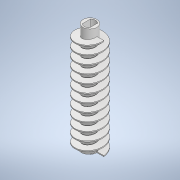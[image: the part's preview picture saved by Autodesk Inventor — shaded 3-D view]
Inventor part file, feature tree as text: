
AUTODESK INVENTOR PART (.ipt)
format: ipt  version: 2022 (Build 260153000, 153)  size: 613,888 bytes
history: native  units: mm
features: sketch x7, extrude x5, other x4, projected_geometry x3, reference x2, mirror x1, sweep x1, chamfer x1
ambient origin geometry x8: Origin, YZ Plane, XZ Plane, XY Plane, X Axis, Y Axis, Z Axis, Center Point
bodies: Solid1 (feature_tree)
feature tree (24):
  extrude  "Extrusion1"  Depth=10.0mm
  sketch  "3D Sketch1"
  extrude  "Extrusion2"  Depth=50.5mm
  mirror  "Mirror1"
  sweep  "Sweep1"
  chamfer  "Chamfer1"  Distance=3.5mm Angle=45.0deg
  extrude  "Extrusion3"  Depth=3.3mm
  extrude  "Extrusion4"  Depth=0.3mm
  extrude  "Extrusion6"  Depth=5.0mm TaperAngle=0.0deg
  sketch  "Sketch1"  dims[d2=0.0mm d3=10.0mm]
  other  "Helical Curve1"
  sketch  "Sketch2"  dims[d6=0.0mm d7=50.5mm]
  projected_geometry  "Projected Loop1"
  sketch  "Sketch3"  dims[d9=0.0mm d10=0.0mm d11=0.0mm d12=3.5mm d13=2.0mm d14=45.0deg]
  projected_geometry  "Projected Loop2"
  sketch  "Sketch4"  dims[d15=4.0mm d16=0.0mm d17=3.3mm]
  projected_geometry  "Projected Loop3"
  sketch  "Sketch5"  dims[d18=15.0mm d19=0.0mm d24=0.3mm]
  sketch  "Sketch7"  dims[d25=0.3mm d26=5.0mm d27=0.0mm]
  reference  "Reference1"
  reference  "Reference2"
  other  "<userpath>\OneDrive - Imperial College London\ROBOICP MK2\solids feeder assembly.iam"
  other  "solids feeder assembly.iam"
  other  "smol stepper:1"
